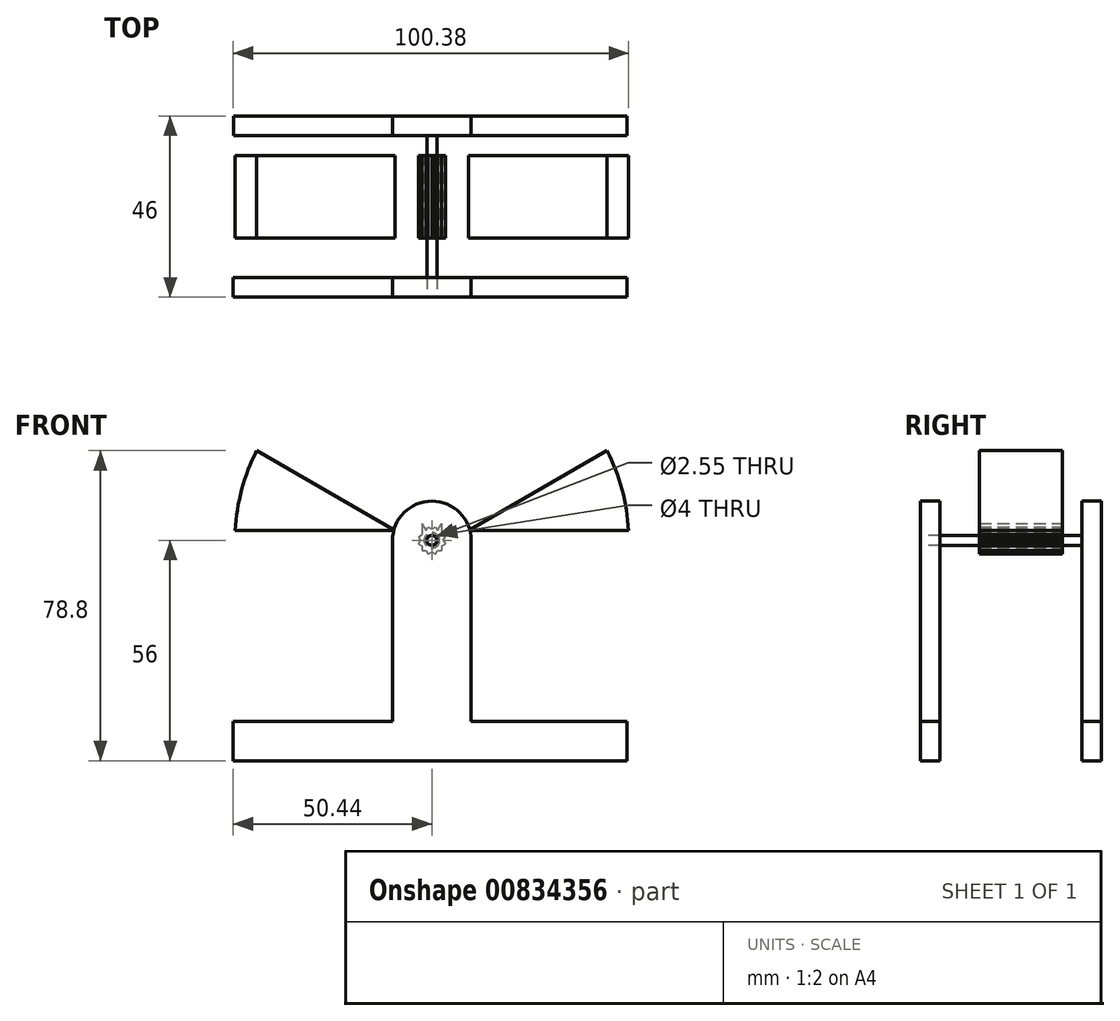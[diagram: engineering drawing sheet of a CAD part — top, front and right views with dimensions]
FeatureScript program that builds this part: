
annotation { "Feature Type Name" : "Feature", "Feature Type Description" : "" }
export const myFeature = defineFeature(function(context is Context, id is Id, definition is map)
    precondition{}
    {
        {
            var Q0;
            Q0=qCreatedBy(makeId("Front.planeOp"),FACE);
            var sketch = newSketch(context, id + "F0", { "sketchPlane" : qUnion([Q0])});
            skCircle(sketch, "E0", {"center": v(0, 0) * mm, "radius": 50 * mm});
            skLineSegment(sketch, "E1", {"start": v(0, 0) * mm, "end": v(0, 50) * mm});
            skLineSegment(sketch, "E2", {"start": v(0, 50) * mm, "end": v(0, -50) * mm});
            skLineSegment(sketch, "E3", {"start": v(-25, 43.3) * mm, "end": v(25, -43.3) * mm});
            skLineSegment(sketch, "E4", {"start": v(-43.3, 25) * mm, "end": v(43.3, -25) * mm});
            skLineSegment(sketch, "E5", {"start": v(-50, 0) * mm, "end": v(50, 0) * mm});
            skLineSegment(sketch, "E6", {"start": v(-43.3, -25) * mm, "end": v(43.3, 25) * mm});
            skLineSegment(sketch, "E7", {"start": v(-25, -43.3) * mm, "end": v(25, 43.3) * mm});
            skLineSegment(sketch, "E8.0", {"start": v(-27.17, 42.05) * mm, "end": v(22.83, -44.55) * mm});
            skLineSegment(sketch, "E9.MirrorCS", {"start": v(-22.83, 44.55) * mm, "end": v(27.17, -42.05) * mm});
            skLineSegment(sketch, "E10.0", {"start": v(-2.5, 50) * mm, "end": v(-2.5, -50) * mm});
            skLineSegment(sketch, "E11.MirrorCS", {"start": v(2.5, 50) * mm, "end": v(2.5, -50) * mm});
            skLineSegment(sketch, "E12.0", {"start": v(-22.83, -44.55) * mm, "end": v(27.17, 42.05) * mm});
            skLineSegment(sketch, "E13.MirrorCS", {"start": v(-27.17, -42.05) * mm, "end": v(22.83, 44.55) * mm});
            skLineSegment(sketch, "E14.0", {"start": v(-44.55, 22.83) * mm, "end": v(42.05, -27.17) * mm});
            skLineSegment(sketch, "E15.MirrorCS", {"start": v(-42.05, 27.17) * mm, "end": v(44.55, -22.83) * mm});
            skLineSegment(sketch, "E16.0", {"start": v(-42.05, -27.17) * mm, "end": v(44.55, 22.83) * mm});
            skLineSegment(sketch, "E17.MirrorCS", {"start": v(-44.55, -22.83) * mm, "end": v(42.05, 27.17) * mm});
            skLineSegment(sketch, "E18.0", {"start": v(-50, -2.5) * mm, "end": v(50, -2.5) * mm});
            skLineSegment(sketch, "E19.MirrorCS", {"start": v(-50, 2.5) * mm, "end": v(50, 2.5) * mm});
            skSolve(sketch);
        }
        {
            var Q0;
            {var subQ3=sQuery(id+"F0.wireOp",EDGE,"E7");var subQ5=sQuery(id+"F0.wireOp",EDGE,"E14.0");var subQ6=makeQuery(id+"F0.imprint","INTERSECT",VERTEX,{"derivedFrom":[subQ3,subQ5]});Q0=makeQuery(id+"F0.imprint","IMPRINT",FACE,{"disambiguationData":[TD([[makeQuery(id+"F0.imprint","IMPRINT",EDGE,{"disambiguationData":[TD([[subQ6,-1.0]])],"derivedFrom":subQ5}),1.0]])]});}
            var Q1;
            {var subQ3=sQuery(id+"F0.wireOp",EDGE,"E3");var subQ5=sQuery(id+"F0.wireOp",EDGE,"E16.0");var subQ6=makeQuery(id+"F0.imprint","INTERSECT",VERTEX,{"derivedFrom":[subQ3,subQ5]});Q1=makeQuery(id+"F0.imprint","IMPRINT",FACE,{"disambiguationData":[TD([[makeQuery(id+"F0.imprint","IMPRINT",EDGE,{"disambiguationData":[TD([[subQ6,1.0]])],"derivedFrom":subQ5}),1.0]])]});}
            var Q2;
            {var subQ3=sQuery(id+"F0.wireOp",EDGE,"E4");var subQ5=sQuery(id+"F0.wireOp",EDGE,"E12.0");var subQ6=makeQuery(id+"F0.imprint","INTERSECT",VERTEX,{"derivedFrom":[subQ3,subQ5]});Q2=makeQuery(id+"F0.imprint","IMPRINT",FACE,{"disambiguationData":[TD([[makeQuery(id+"F0.imprint","IMPRINT",EDGE,{"disambiguationData":[TD([[subQ6,1.0]])],"derivedFrom":subQ5}),1.0]])]});}
            var Q3;
            {var subQ3=sQuery(id+"F0.wireOp",EDGE,"E5");var subQ5=sQuery(id+"F0.wireOp",EDGE,"E11.MirrorCS");var subQ6=makeQuery(id+"F0.imprint","INTERSECT",VERTEX,{"derivedFrom":[subQ3,subQ5]});Q3=makeQuery(id+"F0.imprint","IMPRINT",FACE,{"disambiguationData":[TD([[makeQuery(id+"F0.imprint","IMPRINT",EDGE,{"disambiguationData":[TD([[subQ6,-1.0]])],"derivedFrom":subQ5}),-1.0]])]});}
            var Q4;
            {var subQ3=sQuery(id+"F0.wireOp",EDGE,"E6");var subQ5=sQuery(id+"F0.wireOp",EDGE,"E9.MirrorCS");var subQ6=makeQuery(id+"F0.imprint","INTERSECT",VERTEX,{"derivedFrom":[subQ3,subQ5]});Q4=makeQuery(id+"F0.imprint","IMPRINT",FACE,{"disambiguationData":[TD([[makeQuery(id+"F0.imprint","IMPRINT",EDGE,{"disambiguationData":[TD([[subQ6,-1.0]])],"derivedFrom":subQ5}),-1.0]])]});}
            var Q5;
            {var subQ0=sQuery(id+"F0.wireOp",EDGE,"E9.MirrorCS");var subQ1=sQuery(id+"F0.wireOp",EDGE,"E6");var subQ2=makeQuery(id+"F0.imprint","INTERSECT",VERTEX,{"derivedFrom":[subQ1,subQ0]});Q5=makeQuery(id+"F0.imprint","IMPRINT",FACE,{"disambiguationData":[TD([[makeQuery(id+"F0.imprint","IMPRINT",EDGE,{"disambiguationData":[TD([[subQ2,1.0]])],"derivedFrom":subQ0}),-1.0]])]});}
            var Q6;
            {var subQ3=sQuery(id+"F0.wireOp",EDGE,"E7");var subQ5=sQuery(id+"F0.wireOp",EDGE,"E15.MirrorCS");var subQ6=makeQuery(id+"F0.imprint","INTERSECT",VERTEX,{"derivedFrom":[subQ3,subQ5]});Q6=makeQuery(id+"F0.imprint","IMPRINT",FACE,{"disambiguationData":[TD([[makeQuery(id+"F0.imprint","IMPRINT",EDGE,{"disambiguationData":[TD([[subQ6,1.0]])],"derivedFrom":subQ5}),-1.0]])]});}
            var Q7;
            {var subQ3=sQuery(id+"F0.wireOp",EDGE,"E3");var subQ5=sQuery(id+"F0.wireOp",EDGE,"E17.MirrorCS");var subQ6=makeQuery(id+"F0.imprint","INTERSECT",VERTEX,{"derivedFrom":[subQ3,subQ5]});Q7=makeQuery(id+"F0.imprint","IMPRINT",FACE,{"disambiguationData":[TD([[makeQuery(id+"F0.imprint","IMPRINT",EDGE,{"disambiguationData":[TD([[subQ6,-1.0]])],"derivedFrom":subQ5}),-1.0]])]});}
            var Q8;
            {var subQ3=sQuery(id+"F0.wireOp",EDGE,"E5");var subQ5=sQuery(id+"F0.wireOp",EDGE,"E10.0");var subQ6=makeQuery(id+"F0.imprint","INTERSECT",VERTEX,{"derivedFrom":[subQ3,subQ5]});Q8=makeQuery(id+"F0.imprint","IMPRINT",FACE,{"disambiguationData":[TD([[makeQuery(id+"F0.imprint","IMPRINT",EDGE,{"disambiguationData":[TD([[subQ6,1.0]])],"derivedFrom":subQ5}),1.0]])]});}
            var Q9;
            {var subQ3=sQuery(id+"F0.wireOp",EDGE,"E4");var subQ5=sQuery(id+"F0.wireOp",EDGE,"E13.MirrorCS");var subQ7=makeQuery(id+"F0.imprint","INTERSECT",VERTEX,{"derivedFrom":[subQ3,subQ5]});Q9=makeQuery(id+"F0.imprint","IMPRINT",FACE,{"disambiguationData":[TD([[makeQuery(id+"F0.imprint","IMPRINT",EDGE,{"disambiguationData":[TD([[subQ7,-1.0]])],"derivedFrom":subQ5}),-1.0]])]});}
            var Q10;
            {var subQ3=sQuery(id+"F0.wireOp",EDGE,"E6");var subQ5=sQuery(id+"F0.wireOp",EDGE,"E8.0");var subQ6=makeQuery(id+"F0.imprint","INTERSECT",VERTEX,{"derivedFrom":[subQ3,subQ5]});Q10=makeQuery(id+"F0.imprint","IMPRINT",FACE,{"disambiguationData":[TD([[makeQuery(id+"F0.imprint","IMPRINT",EDGE,{"disambiguationData":[TD([[subQ6,1.0]])],"derivedFrom":subQ5}),1.0]])]});}
            var Q11;
            {var subQ0=sQuery(id+"F0.wireOp",EDGE,"E8.0");var subQ1=sQuery(id+"F0.wireOp",EDGE,"E6");var subQ2=makeQuery(id+"F0.imprint","INTERSECT",VERTEX,{"derivedFrom":[subQ1,subQ0]});Q11=makeQuery(id+"F0.imprint","IMPRINT",FACE,{"disambiguationData":[TD([[makeQuery(id+"F0.imprint","IMPRINT",EDGE,{"disambiguationData":[TD([[subQ2,-1.0]])],"derivedFrom":subQ0}),1.0]])]});}
            var Q12;
            {var subQ0=sQuery(id+"F0.wireOp",EDGE,"E10.0");var subQ1=sQuery(id+"F0.wireOp",EDGE,"E8.0");var subQ2=makeQuery(id+"F0.imprint","INTERSECT",VERTEX,{"derivedFrom":[subQ1,subQ0]});Q12=makeQuery(id+"F0.imprint","IMPRINT",FACE,{"disambiguationData":[TD([[makeQuery(id+"F0.imprint","IMPRINT",EDGE,{"disambiguationData":[TD([[subQ2,1.0]])],"derivedFrom":subQ1}),-1.0]])]});}
            var Q13;
            {var subQ0=sQuery(id+"F0.wireOp",EDGE,"E8.0");var subQ1=sQuery(id+"F0.wireOp",EDGE,"E6");var subQ2=makeQuery(id+"F0.imprint","INTERSECT",VERTEX,{"derivedFrom":[subQ1,subQ0]});Q13=makeQuery(id+"F0.imprint","IMPRINT",FACE,{"disambiguationData":[TD([[makeQuery(id+"F0.imprint","IMPRINT",EDGE,{"disambiguationData":[TD([[subQ2,1.0]])],"derivedFrom":subQ0}),-1.0]])]});}
            var Q14;
            {var subQ0=sQuery(id+"F0.wireOp",EDGE,"E8.0");var subQ1=sQuery(id+"F0.wireOp",EDGE,"E6");var subQ2=makeQuery(id+"F0.imprint","INTERSECT",VERTEX,{"derivedFrom":[subQ1,subQ0]});Q14=makeQuery(id+"F0.imprint","IMPRINT",FACE,{"disambiguationData":[TD([[makeQuery(id+"F0.imprint","IMPRINT",EDGE,{"disambiguationData":[TD([[subQ2,-1.0]])],"derivedFrom":subQ0}),-1.0]])]});}
            var Q15;
            {var subQ0=sQuery(id+"F0.wireOp",EDGE,"E10.0");var subQ1=sQuery(id+"F0.wireOp",EDGE,"E5");var subQ2=makeQuery(id+"F0.imprint","INTERSECT",VERTEX,{"derivedFrom":[subQ1,subQ0]});Q15=makeQuery(id+"F0.imprint","IMPRINT",FACE,{"disambiguationData":[TD([[makeQuery(id+"F0.imprint","IMPRINT",EDGE,{"disambiguationData":[TD([[subQ2,-1.0]])],"derivedFrom":subQ0}),-1.0]])]});}
            var Q16;
            {var subQ0=sQuery(id+"F0.wireOp",EDGE,"E10.0");var subQ1=sQuery(id+"F0.wireOp",EDGE,"E5");var subQ2=makeQuery(id+"F0.imprint","INTERSECT",VERTEX,{"derivedFrom":[subQ1,subQ0]});Q16=makeQuery(id+"F0.imprint","IMPRINT",FACE,{"disambiguationData":[TD([[makeQuery(id+"F0.imprint","IMPRINT",EDGE,{"disambiguationData":[TD([[subQ2,1.0]])],"derivedFrom":subQ0}),-1.0]])]});}
            var Q17;
            {var subQ0=sQuery(id+"F0.wireOp",EDGE,"E17.MirrorCS");var subQ1=sQuery(id+"F0.wireOp",EDGE,"E8.0");var subQ2=makeQuery(id+"F0.imprint","INTERSECT",VERTEX,{"derivedFrom":[subQ1,subQ0]});Q17=makeQuery(id+"F0.imprint","IMPRINT",FACE,{"disambiguationData":[TD([[makeQuery(id+"F0.imprint","IMPRINT",EDGE,{"disambiguationData":[TD([[subQ2,-1.0]])],"derivedFrom":subQ1}),1.0]])]});}
            var Q18;
            {var subQ0=sQuery(id+"F0.wireOp",EDGE,"E13.MirrorCS");var subQ1=sQuery(id+"F0.wireOp",EDGE,"E4");var subQ2=makeQuery(id+"F0.imprint","INTERSECT",VERTEX,{"derivedFrom":[subQ1,subQ0]});Q18=makeQuery(id+"F0.imprint","IMPRINT",FACE,{"disambiguationData":[TD([[makeQuery(id+"F0.imprint","IMPRINT",EDGE,{"disambiguationData":[TD([[subQ2,1.0]])],"derivedFrom":subQ0}),1.0]])]});}
            var Q19;
            {var subQ0=sQuery(id+"F0.wireOp",EDGE,"E13.MirrorCS");var subQ1=sQuery(id+"F0.wireOp",EDGE,"E4");var subQ2=makeQuery(id+"F0.imprint","INTERSECT",VERTEX,{"derivedFrom":[subQ1,subQ0]});Q19=makeQuery(id+"F0.imprint","IMPRINT",FACE,{"disambiguationData":[TD([[makeQuery(id+"F0.imprint","IMPRINT",EDGE,{"disambiguationData":[TD([[subQ2,-1.0]])],"derivedFrom":subQ0}),1.0]])]});}
            var Q20;
            {var subQ0=sQuery(id+"F0.wireOp",EDGE,"E17.MirrorCS");var subQ1=sQuery(id+"F0.wireOp",EDGE,"E3");var subQ2=makeQuery(id+"F0.imprint","INTERSECT",VERTEX,{"derivedFrom":[subQ1,subQ0]});Q20=makeQuery(id+"F0.imprint","IMPRINT",FACE,{"disambiguationData":[TD([[makeQuery(id+"F0.imprint","IMPRINT",EDGE,{"disambiguationData":[TD([[subQ2,1.0]])],"derivedFrom":subQ0}),1.0]])]});}
            var Q21;
            {var subQ0=sQuery(id+"F0.wireOp",EDGE,"E17.MirrorCS");var subQ1=sQuery(id+"F0.wireOp",EDGE,"E3");var subQ2=makeQuery(id+"F0.imprint","INTERSECT",VERTEX,{"derivedFrom":[subQ1,subQ0]});Q21=makeQuery(id+"F0.imprint","IMPRINT",FACE,{"disambiguationData":[TD([[makeQuery(id+"F0.imprint","IMPRINT",EDGE,{"disambiguationData":[TD([[subQ2,-1.0]])],"derivedFrom":subQ0}),1.0]])]});}
            var Q22;
            {var subQ0=sQuery(id+"F0.wireOp",EDGE,"E19.MirrorCS");var subQ1=sQuery(id+"F0.wireOp",EDGE,"E10.0");var subQ2=makeQuery(id+"F0.imprint","INTERSECT",VERTEX,{"derivedFrom":[subQ1,subQ0]});Q22=makeQuery(id+"F0.imprint","IMPRINT",FACE,{"disambiguationData":[TD([[makeQuery(id+"F0.imprint","IMPRINT",EDGE,{"disambiguationData":[TD([[subQ2,-1.0]])],"derivedFrom":subQ1}),1.0]])]});}
            var Q23;
            {var subQ0=sQuery(id+"F0.wireOp",EDGE,"E15.MirrorCS");var subQ1=sQuery(id+"F0.wireOp",EDGE,"E13.MirrorCS");var subQ2=makeQuery(id+"F0.imprint","INTERSECT",VERTEX,{"derivedFrom":[subQ1,subQ0]});Q23=makeQuery(id+"F0.imprint","IMPRINT",FACE,{"disambiguationData":[TD([[makeQuery(id+"F0.imprint","IMPRINT",EDGE,{"disambiguationData":[TD([[subQ2,1.0]])],"derivedFrom":subQ1}),-1.0]])]});}
            var Q24;
            {var subQ0=sQuery(id+"F0.wireOp",EDGE,"E19.MirrorCS");var subQ1=sQuery(id+"F0.wireOp",EDGE,"E2");var subQ2=makeQuery(id+"F0.imprint","INTERSECT",VERTEX,{"derivedFrom":[subQ1,subQ0]});Q24=makeQuery(id+"F0.imprint","IMPRINT",FACE,{"disambiguationData":[TD([[makeQuery(id+"F0.imprint","IMPRINT",EDGE,{"disambiguationData":[TD([[subQ2,1.0]])],"derivedFrom":subQ0}),1.0]])]});}
            var Q25;
            {var subQ0=sQuery(id+"F0.wireOp",EDGE,"E19.MirrorCS");var subQ1=sQuery(id+"F0.wireOp",EDGE,"E2");var subQ2=makeQuery(id+"F0.imprint","INTERSECT",VERTEX,{"derivedFrom":[subQ1,subQ0]});Q25=makeQuery(id+"F0.imprint","IMPRINT",FACE,{"disambiguationData":[TD([[makeQuery(id+"F0.imprint","IMPRINT",EDGE,{"disambiguationData":[TD([[subQ2,-1.0]])],"derivedFrom":subQ0}),1.0]])]});}
            var Q26;
            {var subQ0=sQuery(id+"F0.wireOp",EDGE,"E17.MirrorCS");var subQ1=sQuery(id+"F0.wireOp",EDGE,"E9.MirrorCS");var subQ2=makeQuery(id+"F0.imprint","INTERSECT",VERTEX,{"derivedFrom":[subQ1,subQ0]});Q26=makeQuery(id+"F0.imprint","IMPRINT",FACE,{"disambiguationData":[TD([[makeQuery(id+"F0.imprint","IMPRINT",EDGE,{"disambiguationData":[TD([[subQ2,-1.0]])],"derivedFrom":subQ1}),-1.0]])]});}
            var Q27;
            {var subQ0=sQuery(id+"F0.wireOp",EDGE,"E15.MirrorCS");var subQ1=sQuery(id+"F0.wireOp",EDGE,"E7");var subQ2=makeQuery(id+"F0.imprint","INTERSECT",VERTEX,{"derivedFrom":[subQ1,subQ0]});Q27=makeQuery(id+"F0.imprint","IMPRINT",FACE,{"disambiguationData":[TD([[makeQuery(id+"F0.imprint","IMPRINT",EDGE,{"disambiguationData":[TD([[subQ2,-1.0]])],"derivedFrom":subQ0}),1.0]])]});}
            var Q28;
            {var subQ0=sQuery(id+"F0.wireOp",EDGE,"E15.MirrorCS");var subQ1=sQuery(id+"F0.wireOp",EDGE,"E7");var subQ2=makeQuery(id+"F0.imprint","INTERSECT",VERTEX,{"derivedFrom":[subQ1,subQ0]});Q28=makeQuery(id+"F0.imprint","IMPRINT",FACE,{"disambiguationData":[TD([[makeQuery(id+"F0.imprint","IMPRINT",EDGE,{"disambiguationData":[TD([[subQ2,1.0]])],"derivedFrom":subQ0}),1.0]])]});}
            var Q29;
            {var subQ0=sQuery(id+"F0.wireOp",EDGE,"E9.MirrorCS");var subQ1=sQuery(id+"F0.wireOp",EDGE,"E6");var subQ2=makeQuery(id+"F0.imprint","INTERSECT",VERTEX,{"derivedFrom":[subQ1,subQ0]});Q29=makeQuery(id+"F0.imprint","IMPRINT",FACE,{"disambiguationData":[TD([[makeQuery(id+"F0.imprint","IMPRINT",EDGE,{"disambiguationData":[TD([[subQ2,1.0]])],"derivedFrom":subQ0}),1.0]])]});}
            var Q30;
            {var subQ0=sQuery(id+"F0.wireOp",EDGE,"E9.MirrorCS");var subQ1=sQuery(id+"F0.wireOp",EDGE,"E6");var subQ2=makeQuery(id+"F0.imprint","INTERSECT",VERTEX,{"derivedFrom":[subQ1,subQ0]});Q30=makeQuery(id+"F0.imprint","IMPRINT",FACE,{"disambiguationData":[TD([[makeQuery(id+"F0.imprint","IMPRINT",EDGE,{"disambiguationData":[TD([[subQ2,-1.0]])],"derivedFrom":subQ0}),1.0]])]});}
            var Q31;
            {var subQ0=sQuery(id+"F0.wireOp",EDGE,"E15.MirrorCS");var subQ1=sQuery(id+"F0.wireOp",EDGE,"E9.MirrorCS");var subQ2=makeQuery(id+"F0.imprint","INTERSECT",VERTEX,{"derivedFrom":[subQ1,subQ0]});Q31=makeQuery(id+"F0.imprint","IMPRINT",FACE,{"disambiguationData":[TD([[makeQuery(id+"F0.imprint","IMPRINT",EDGE,{"disambiguationData":[TD([[subQ2,1.0]])],"derivedFrom":subQ1}),1.0]])]});}
            var Q32;
            {var subQ0=sQuery(id+"F0.wireOp",EDGE,"E11.MirrorCS");var subQ1=sQuery(id+"F0.wireOp",EDGE,"E9.MirrorCS");var subQ2=makeQuery(id+"F0.imprint","INTERSECT",VERTEX,{"derivedFrom":[subQ1,subQ0]});Q32=makeQuery(id+"F0.imprint","IMPRINT",FACE,{"disambiguationData":[TD([[makeQuery(id+"F0.imprint","IMPRINT",EDGE,{"disambiguationData":[TD([[subQ2,-1.0]])],"derivedFrom":subQ1}),1.0]])]});}
            var Q33;
            {var subQ0=sQuery(id+"F0.wireOp",EDGE,"E11.MirrorCS");var subQ1=sQuery(id+"F0.wireOp",EDGE,"E5");var subQ2=makeQuery(id+"F0.imprint","INTERSECT",VERTEX,{"derivedFrom":[subQ1,subQ0]});Q33=makeQuery(id+"F0.imprint","IMPRINT",FACE,{"disambiguationData":[TD([[makeQuery(id+"F0.imprint","IMPRINT",EDGE,{"disambiguationData":[TD([[subQ2,-1.0]])],"derivedFrom":subQ0}),1.0]])]});}
            var Q34;
            {var subQ0=sQuery(id+"F0.wireOp",EDGE,"E11.MirrorCS");var subQ1=sQuery(id+"F0.wireOp",EDGE,"E5");var subQ2=makeQuery(id+"F0.imprint","INTERSECT",VERTEX,{"derivedFrom":[subQ1,subQ0]});Q34=makeQuery(id+"F0.imprint","IMPRINT",FACE,{"disambiguationData":[TD([[makeQuery(id+"F0.imprint","IMPRINT",EDGE,{"disambiguationData":[TD([[subQ2,1.0]])],"derivedFrom":subQ0}),1.0]])]});}
            var Q35;
            {var subQ0=sQuery(id+"F0.wireOp",EDGE,"E16.0");var subQ1=sQuery(id+"F0.wireOp",EDGE,"E9.MirrorCS");var subQ2=makeQuery(id+"F0.imprint","INTERSECT",VERTEX,{"derivedFrom":[subQ1,subQ0]});Q35=makeQuery(id+"F0.imprint","IMPRINT",FACE,{"disambiguationData":[TD([[makeQuery(id+"F0.imprint","IMPRINT",EDGE,{"disambiguationData":[TD([[subQ2,1.0]])],"derivedFrom":subQ1}),-1.0]])]});}
            var Q36;
            {var subQ0=sQuery(id+"F0.wireOp",EDGE,"E12.0");var subQ1=sQuery(id+"F0.wireOp",EDGE,"E4");var subQ2=makeQuery(id+"F0.imprint","INTERSECT",VERTEX,{"derivedFrom":[subQ1,subQ0]});Q36=makeQuery(id+"F0.imprint","IMPRINT",FACE,{"disambiguationData":[TD([[makeQuery(id+"F0.imprint","IMPRINT",EDGE,{"disambiguationData":[TD([[subQ2,-1.0]])],"derivedFrom":subQ0}),-1.0]])]});}
            var Q37;
            {var subQ0=sQuery(id+"F0.wireOp",EDGE,"E12.0");var subQ1=sQuery(id+"F0.wireOp",EDGE,"E4");var subQ2=makeQuery(id+"F0.imprint","INTERSECT",VERTEX,{"derivedFrom":[subQ1,subQ0]});Q37=makeQuery(id+"F0.imprint","IMPRINT",FACE,{"disambiguationData":[TD([[makeQuery(id+"F0.imprint","IMPRINT",EDGE,{"disambiguationData":[TD([[subQ2,1.0]])],"derivedFrom":subQ0}),-1.0]])]});}
            var Q38;
            {var subQ0=sQuery(id+"F0.wireOp",EDGE,"E18.0");var subQ1=sQuery(id+"F0.wireOp",EDGE,"E11.MirrorCS");var subQ2=makeQuery(id+"F0.imprint","INTERSECT",VERTEX,{"derivedFrom":[subQ1,subQ0]});Q38=makeQuery(id+"F0.imprint","IMPRINT",FACE,{"disambiguationData":[TD([[makeQuery(id+"F0.imprint","IMPRINT",EDGE,{"disambiguationData":[TD([[subQ2,1.0]])],"derivedFrom":subQ1}),-1.0]])]});}
            var Q39;
            {var subQ0=sQuery(id+"F0.wireOp",EDGE,"E16.0");var subQ1=sQuery(id+"F0.wireOp",EDGE,"E3");var subQ2=makeQuery(id+"F0.imprint","INTERSECT",VERTEX,{"derivedFrom":[subQ1,subQ0]});Q39=makeQuery(id+"F0.imprint","IMPRINT",FACE,{"disambiguationData":[TD([[makeQuery(id+"F0.imprint","IMPRINT",EDGE,{"disambiguationData":[TD([[subQ2,-1.0]])],"derivedFrom":subQ0}),-1.0]])]});}
            var Q40;
            {var subQ0=sQuery(id+"F0.wireOp",EDGE,"E16.0");var subQ1=sQuery(id+"F0.wireOp",EDGE,"E3");var subQ2=makeQuery(id+"F0.imprint","INTERSECT",VERTEX,{"derivedFrom":[subQ1,subQ0]});Q40=makeQuery(id+"F0.imprint","IMPRINT",FACE,{"disambiguationData":[TD([[makeQuery(id+"F0.imprint","IMPRINT",EDGE,{"disambiguationData":[TD([[subQ2,1.0]])],"derivedFrom":subQ0}),-1.0]])]});}
            var Q41;
            {var subQ0=sQuery(id+"F0.wireOp",EDGE,"E14.0");var subQ1=sQuery(id+"F0.wireOp",EDGE,"E12.0");var subQ2=makeQuery(id+"F0.imprint","INTERSECT",VERTEX,{"derivedFrom":[subQ1,subQ0]});Q41=makeQuery(id+"F0.imprint","IMPRINT",FACE,{"disambiguationData":[TD([[makeQuery(id+"F0.imprint","IMPRINT",EDGE,{"disambiguationData":[TD([[subQ2,-1.0]])],"derivedFrom":subQ1}),1.0]])]});}
            var Q42;
            {var subQ0=sQuery(id+"F0.wireOp",EDGE,"E18.0");var subQ1=sQuery(id+"F0.wireOp",EDGE,"E2");var subQ2=makeQuery(id+"F0.imprint","INTERSECT",VERTEX,{"derivedFrom":[subQ1,subQ0]});Q42=makeQuery(id+"F0.imprint","IMPRINT",FACE,{"disambiguationData":[TD([[makeQuery(id+"F0.imprint","IMPRINT",EDGE,{"disambiguationData":[TD([[subQ2,-1.0]])],"derivedFrom":subQ0}),-1.0]])]});}
            var Q43;
            {var subQ0=sQuery(id+"F0.wireOp",EDGE,"E18.0");var subQ1=sQuery(id+"F0.wireOp",EDGE,"E2");var subQ2=makeQuery(id+"F0.imprint","INTERSECT",VERTEX,{"derivedFrom":[subQ1,subQ0]});Q43=makeQuery(id+"F0.imprint","IMPRINT",FACE,{"disambiguationData":[TD([[makeQuery(id+"F0.imprint","IMPRINT",EDGE,{"disambiguationData":[TD([[subQ2,1.0]])],"derivedFrom":subQ0}),-1.0]])]});}
            var Q44;
            {var subQ0=sQuery(id+"F0.wireOp",EDGE,"E16.0");var subQ1=sQuery(id+"F0.wireOp",EDGE,"E8.0");var subQ2=makeQuery(id+"F0.imprint","INTERSECT",VERTEX,{"derivedFrom":[subQ1,subQ0]});Q44=makeQuery(id+"F0.imprint","IMPRINT",FACE,{"disambiguationData":[TD([[makeQuery(id+"F0.imprint","IMPRINT",EDGE,{"disambiguationData":[TD([[subQ2,1.0]])],"derivedFrom":subQ1}),1.0]])]});}
            var Q45;
            {var subQ0=sQuery(id+"F0.wireOp",EDGE,"E14.0");var subQ1=sQuery(id+"F0.wireOp",EDGE,"E7");var subQ2=makeQuery(id+"F0.imprint","INTERSECT",VERTEX,{"derivedFrom":[subQ1,subQ0]});Q45=makeQuery(id+"F0.imprint","IMPRINT",FACE,{"disambiguationData":[TD([[makeQuery(id+"F0.imprint","IMPRINT",EDGE,{"disambiguationData":[TD([[subQ2,-1.0]])],"derivedFrom":subQ0}),-1.0]])]});}
            var Q46;
            {var subQ0=sQuery(id+"F0.wireOp",EDGE,"E14.0");var subQ1=sQuery(id+"F0.wireOp",EDGE,"E7");var subQ2=makeQuery(id+"F0.imprint","INTERSECT",VERTEX,{"derivedFrom":[subQ1,subQ0]});Q46=makeQuery(id+"F0.imprint","IMPRINT",FACE,{"disambiguationData":[TD([[makeQuery(id+"F0.imprint","IMPRINT",EDGE,{"disambiguationData":[TD([[subQ2,1.0]])],"derivedFrom":subQ0}),-1.0]])]});}
            var Q47;
            {var subQ0=sQuery(id+"F0.wireOp",EDGE,"E14.0");var subQ1=sQuery(id+"F0.wireOp",EDGE,"E8.0");var subQ2=makeQuery(id+"F0.imprint","INTERSECT",VERTEX,{"derivedFrom":[subQ1,subQ0]});Q47=makeQuery(id+"F0.imprint","IMPRINT",FACE,{"disambiguationData":[TD([[makeQuery(id+"F0.imprint","IMPRINT",EDGE,{"disambiguationData":[TD([[subQ2,-1.0]])],"derivedFrom":subQ1}),-1.0]])]});}
            extrude(context, id + "F1", {"entities" : qUnion([Q0, Q1, Q2, Q3, Q4, Q5, Q6, Q7, Q8, Q9, Q10, Q11, Q12, Q13, Q14, Q15, Q16, Q17, Q18, Q19, Q20, Q21, Q22, Q23, Q24, Q25, Q26, Q27, Q28, Q29, Q30, Q31, Q32, Q33, Q34, Q35, Q36, Q37, Q38, Q39, Q40, Q41, Q42, Q43, Q44, Q45, Q46, Q47]), "depth" : 21 * mm, "offsetDistance" : 25 * mm});
        }
        {
            var Q0;
            Q0=qCreatedBy(makeId("Front.planeOp"),FACE);
            var sketch = newSketch(context, id + "F2", { "sketchPlane" : qUnion([Q0])});
            skCircle(sketch, "E20", {"center": v(0, 0) * mm, "radius": 2 * mm});
            skSolve(sketch);
        }
        {
            var Q0;
            Q0 = qSketchRegion(id + "F2", true);
            extrude(context, id + "F3", {"entities" : qUnion([Q0]), "operationType" : NewBodyOperationType.REMOVE, "endBound" : BoundingType.THROUGH_ALL, "depth" : 25 * mm, "offsetDistance" : 25 * mm});
        }
        {
            var Q0;
            Q0=qCreatedBy(makeId("Front.planeOp"),FACE);
            var sketch = newSketch(context, id + "F4", { "sketchPlane" : qUnion([Q0])});
            skCircle(sketch, "E21", {"center": v(0, 0) * mm, "radius": 1.93 * mm});
            skSolve(sketch);
        }
        {
            var Q0;
            Q0 = qSketchRegion(id + "F4", true);
            extrude(context, id + "F5", {"entities" : qUnion([Q0]), "depth" : 21 * mm, "offsetDistance" : 25 * mm});
        }
        {
            var Q0;
            Q0=makeQuery(id+"F5.opExtrude","CAP_FACE",FACE,{"disambiguationData":[OSD([sQuery(id+"F4.wireOp",EDGE,"E21")])],"isStart":false});
            var sketch = newSketch(context, id + "F6", { "sketchPlane" : qUnion([Q0])});
            skCircle(sketch, "E22", {"center": v(0, 0) * mm, "radius": 1.25 * mm});
            skSolve(sketch);
        }
        {
            var Q0;
            Q0 = qSketchRegion(id + "F6", true);
            extrude(context, id + "F7", {"entities" : qUnion([Q0]), "operationType" : NewBodyOperationType.ADD, "depth" : 10 * mm, "offsetDistance" : 25 * mm});
        }
        {
            var Q0;
            Q0=makeQuery(id+"F5.opExtrude","CAP_FACE",FACE,{"disambiguationData":[OSD([sQuery(id+"F4.wireOp",EDGE,"E21")])],"isStart":true});
            var sketch = newSketch(context, id + "F8", { "sketchPlane" : qUnion([Q0])});
            skCircle(sketch, "E23", {"center": v(0, 0) * mm, "radius": 1.25 * mm});
            skSolve(sketch);
        }
        {
            var Q0;
            Q0 = qSketchRegion(id + "F8", true);
            extrude(context, id + "F9", {"entities" : qUnion([Q0]), "operationType" : NewBodyOperationType.ADD, "depth" : 5 * mm, "offsetDistance" : 25 * mm});
        }
        {
            var Q0;
            Q0=makeQuery(id+"F9.opExtrude","CAP_FACE",FACE,{"disambiguationData":[OSD([sQuery(id+"F8.wireOp",EDGE,"E23")])],"isStart":false});
            var sketch = newSketch(context, id + "F10", { "sketchPlane" : qUnion([Q0])});
            skCircle(sketch, "E24", {"center": v(0, 0) * mm, "radius": 10 * mm});
            skSolve(sketch);
        }
        {
            var Q0;
            Q0 = qSketchRegion(id + "F10", true);
            extrude(context, id + "F11", {"entities" : qUnion([Q0]), "operationType" : NewBodyOperationType.ADD, "depth" : 5 * mm, "offsetDistance" : 25 * mm});
        }
        {
            var Q0;
            Q0=makeQuery(id+"F7.opExtrude","CAP_FACE",FACE,{"disambiguationData":[OSD([sQuery(id+"F6.wireOp",EDGE,"E22")])],"isStart":false});
            var sketch = newSketch(context, id + "F12", { "sketchPlane" : qUnion([Q0])});
            skCircle(sketch, "E25", {"center": v(0, 0) * mm, "radius": 10 * mm});
            skSolve(sketch);
        }
        {
            var Q0;
            Q0 = qSketchRegion(id + "F12", true);
            extrude(context, id + "F13", {"entities" : qUnion([Q0]), "operationType" : NewBodyOperationType.ADD, "depth" : 5 * mm, "offsetDistance" : 25 * mm});
        }
        {
            var Q0;
            Q0=makeQuery(id+"F13.opExtrude","CAP_FACE",FACE,{"disambiguationData":[OSD([sQuery(id+"F12.wireOp",EDGE,"E25")])],"isStart":false});
            var sketch = newSketch(context, id + "F14", { "sketchPlane" : qUnion([Q0])});
            skCircle(sketch, "E26", {"center": v(0, 0) * mm, "radius": 1.28 * mm});
            skSolve(sketch);
        }
        {
            var Q0;
            Q0 = qSketchRegion(id + "F14", true);
            extrude(context, id + "F15", {"entities" : qUnion([Q0]), "operationType" : NewBodyOperationType.REMOVE, "oppositeDirection" : true, "depth" : 5 * mm, "offsetDistance" : 25 * mm});
        }
        {
            var Q0;
            Q0=makeQuery(id+"F11.opExtrude","CAP_FACE",FACE,{"disambiguationData":[OSD([sQuery(id+"F10.wireOp",EDGE,"E24")])],"isStart":false});
            var sketch = newSketch(context, id + "F16", { "sketchPlane" : qUnion([Q0])});
            skSolve(sketch);
        }
        {
            var Q0;
            Q0=makeQuery(id+"F13.opExtrude","CAP_FACE",FACE,{"disambiguationData":[OSD([sQuery(id+"F12.wireOp",EDGE,"E25")])],"isStart":false});
            var sketch = newSketch(context, id + "F17", { "sketchPlane" : qUnion([Q0])});
            skLineSegment(sketch, "E27", {"start": v(0, 0) * mm, "end": v(0, -56) * mm});
            skLineSegment(sketch, "E28.0", {"start": v(-10, 0) * mm, "end": v(-10, -56) * mm});
            skLineSegment(sketch, "E29.MirrorCS", {"start": v(10, 0) * mm, "end": v(10, -56) * mm});
            skLineSegment(sketch, "E30", {"start": v(-10, 0) * mm, "end": v(10, 0) * mm});
            skLineSegment(sketch, "E31", {"start": v(10, -56) * mm, "end": v(-10, -56) * mm});
            skSolve(sketch);
        }
        {
            var Q0;
            Q0 = qSketchRegion(id + "F17", true);
            extrude(context, id + "F18", {"entities" : qUnion([Q0]), "oppositeDirection" : true, "depth" : 5 * mm, "offsetDistance" : 25 * mm});
        }
        {
            var Q0;
            Q0=makeQuery(id+"F13.opExtrude","CAP_FACE",FACE,{"disambiguationData":[OSD([sQuery(id+"F12.wireOp",EDGE,"E25")])],"isStart":false});
            var sketch = newSketch(context, id + "F19", { "sketchPlane" : qUnion([Q0])});
            skCircle(sketch, "E32", {"center": v(0, 0) * mm, "radius": 1.28 * mm});
            skSolve(sketch);
        }
        {
            var Q0;
            Q0 = qSketchRegion(id + "F19", true);
            extrude(context, id + "F20", {"entities" : qUnion([Q0]), "operationType" : NewBodyOperationType.REMOVE, "oppositeDirection" : true, "depth" : 5 * mm, "offsetDistance" : 25 * mm});
        }
        {
            var Q0;
            Q0=makeQuery(id+"F18.opExtrude","SWEPT_BODY",BODY,{"disambiguationData":[OSD([sQuery(id+"F17.wireOp",EDGE,"E28.0"),sQuery(id+"F17.wireOp",EDGE,"E29.MirrorCS"),sQuery(id+"F17.wireOp",EDGE,"E30"),sQuery(id+"F17.wireOp",EDGE,"E31")])]});
            var Q1;
            Q1=makeQuery(id+"F15.boolean.opBoolean","SPLIT",BODY,{"disambiguationData":[OD(1.0)],"derivedFrom":makeQuery(id+"F5.opExtrude","SWEPT_BODY",BODY,{"disambiguationData":[OSD([sQuery(id+"F4.wireOp",EDGE,"E21")])]})});
            booleanBodies(context, id + "F21", {"operationType" : BooleanOperationType.UNION, "tools" : qUnion([Q0, Q1])});
        }
        {
            var Q0;
            Q0=makeQuery(id+"F16.imprint","IMPRINT",FACE,{"disambiguationData":[TD([[makeQuery(id+"F16.imprint","IMPRINT",EDGE,{"derivedFrom":makeQuery(id+"F11.opExtrude","CAP_EDGE",EDGE,{"disambiguationData":[OSD([sQuery(id+"F10.wireOp",EDGE,"E24")])],"isStart":false})}),1.0]])]});
            var sketch = newSketch(context, id + "F22", { "sketchPlane" : qUnion([Q0])});
            skLineSegment(sketch, "E33", {"start": v(0, 0) * mm, "end": v(0, -56) * mm});
            skLineSegment(sketch, "E34.0", {"start": v(-10, 0) * mm, "end": v(-10, -56) * mm});
            skLineSegment(sketch, "E35.MirrorCS", {"start": v(10, 0) * mm, "end": v(10, -56) * mm});
            skLineSegment(sketch, "E36", {"start": v(-10, 0) * mm, "end": v(10, 0) * mm});
            skLineSegment(sketch, "E37", {"start": v(10, -56) * mm, "end": v(-10, -56) * mm});
            skSolve(sketch);
        }
        {
            var Q0;
            Q0 = qSketchRegion(id + "F22", true);
            extrude(context, id + "F23", {"entities" : qUnion([Q0]), "operationType" : NewBodyOperationType.ADD, "oppositeDirection" : true, "depth" : 5 * mm, "offsetDistance" : 25 * mm});
        }
        {
            var Q0;
            Q0=makeQuery(id+"F21.opBoolean","MERGE",FACE,{"derivedFrom":[makeQuery(id+"F13.opExtrude","CAP_FACE",FACE,{"disambiguationData":[OSD([sQuery(id+"F12.wireOp",EDGE,"E25")])],"isStart":false}),makeQuery(id+"F18.opExtrude","CAP_FACE",FACE,{"disambiguationData":[OSD([sQuery(id+"F17.wireOp",EDGE,"E28.0"),sQuery(id+"F17.wireOp",EDGE,"E29.MirrorCS"),sQuery(id+"F17.wireOp",EDGE,"E30"),sQuery(id+"F17.wireOp",EDGE,"E31")])],"isStart":true})]});
            var sketch = newSketch(context, id + "F24", { "sketchPlane" : qUnion([Q0])});
            skLineSegment(sketch, "E38", {"start": v(0, -56) * mm, "end": v(49.56, -56) * mm});
            skLineSegment(sketch, "E39", {"start": v(49.56, -56) * mm, "end": v(-50.44, -56) * mm});
            skLineSegment(sketch, "E40.0", {"start": v(49.56, -46) * mm, "end": v(-50.44, -46) * mm});
            skLineSegment(sketch, "E41", {"start": v(-50.44, -56) * mm, "end": v(-50.44, -46) * mm});
            skLineSegment(sketch, "E42", {"start": v(49.56, -46) * mm, "end": v(49.56, -56) * mm});
            skSolve(sketch);
        }
        {
            var Q0;
            Q0 = qSketchRegion(id + "F24", true);
            extrude(context, id + "F25", {"entities" : qUnion([Q0]), "operationType" : NewBodyOperationType.ADD, "oppositeDirection" : true, "depth" : 5 * mm, "offsetDistance" : 25 * mm});
        }
        {
            var Q0;
            Q0=makeQuery(id+"F23.boolean.opBoolean","MERGE",FACE,{"derivedFrom":[makeQuery(id+"F11.opExtrude","CAP_FACE",FACE,{"disambiguationData":[OSD([sQuery(id+"F10.wireOp",EDGE,"E24")])],"isStart":false}),makeQuery(id+"F23.opExtrude","CAP_FACE",FACE,{"disambiguationData":[OSD([sQuery(id+"F22.wireOp",EDGE,"E34.0"),sQuery(id+"F22.wireOp",EDGE,"E35.MirrorCS"),sQuery(id+"F22.wireOp",EDGE,"E36"),sQuery(id+"F22.wireOp",EDGE,"E37")])],"isStart":true})]});
            var sketch = newSketch(context, id + "F26", { "sketchPlane" : qUnion([Q0])});
            skLineSegment(sketch, "E43", {"start": v(0, -56) * mm, "end": v(-49.63, -56) * mm});
            skLineSegment(sketch, "E44", {"start": v(-49.63, -56) * mm, "end": v(50.37, -56) * mm});
            skLineSegment(sketch, "E45.0", {"start": v(-49.63, -46) * mm, "end": v(50.37, -46) * mm});
            skLineSegment(sketch, "E46", {"start": v(-49.63, -56) * mm, "end": v(-49.63, -46) * mm});
            skLineSegment(sketch, "E47", {"start": v(50.37, -46) * mm, "end": v(50.37, -56) * mm});
            skSolve(sketch);
        }
        {
            var Q0;
            Q0 = qSketchRegion(id + "F26", true);
            extrude(context, id + "F27", {"entities" : qUnion([Q0]), "operationType" : NewBodyOperationType.ADD, "oppositeDirection" : true, "depth" : 5 * mm, "offsetDistance" : 25 * mm});
        }
    });
